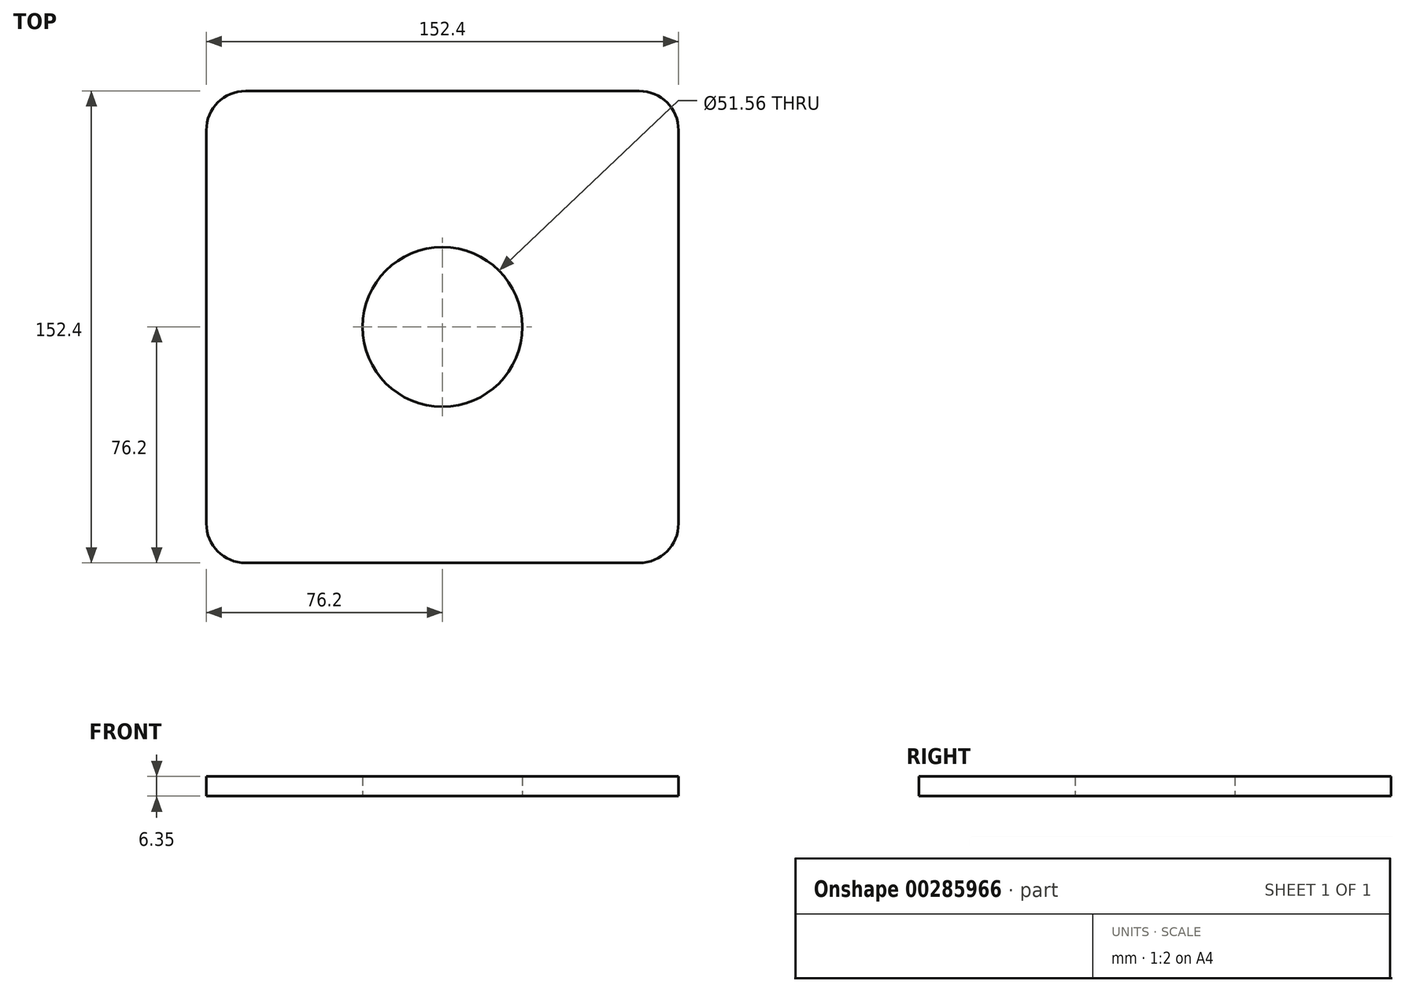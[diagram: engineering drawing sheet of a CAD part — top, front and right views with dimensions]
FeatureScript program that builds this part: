
annotation { "Feature Type Name" : "Feature", "Feature Type Description" : "" }
export const myFeature = defineFeature(function(context is Context, id is Id, definition is map)
    precondition{}
    {
        {
            var Q0;
            Q0=qCreatedBy(makeId("Top.planeOp"),FACE);
            var sketch = newSketch(context, id + "F0", { "sketchPlane" : qUnion([Q0])});
            skLineSegment(sketch, "E0.bottom", {"start": v(12.7, 0) * mm, "end": v(139.7, 0) * mm});
            skLineSegment(sketch, "E0.top", {"start": v(12.7, -152.4) * mm, "end": v(139.7, -152.4) * mm});
            skLineSegment(sketch, "E0.left", {"start": v(0, -12.7) * mm, "end": v(0, -139.7) * mm});
            skLineSegment(sketch, "E0.right", {"start": v(152.4, -12.7) * mm, "end": v(152.4, -139.7) * mm});
            skPoint(sketch, "E1.visualSharp", {"position": v(0, 0) * mm});
            skArc(sketch, "E1.filletArc", {"start": v(12.7, 0) * mm, "mid": v(3.72, -3.72) * mm, "end": v(0, -12.7) * mm});
            skPoint(sketch, "E2.visualSharp", {"position": v(152.4, 0) * mm});
            skArc(sketch, "E2.filletArc", {"start": v(152.4, -12.7) * mm, "mid": v(148.68, -3.72) * mm, "end": v(139.7, 0) * mm});
            skPoint(sketch, "E3.visualSharp", {"position": v(152.4, -152.4) * mm});
            skArc(sketch, "E3.filletArc", {"start": v(139.7, -152.4) * mm, "mid": v(148.68, -148.68) * mm, "end": v(152.4, -139.7) * mm});
            skPoint(sketch, "E4.visualSharp", {"position": v(0, -152.4) * mm});
            skArc(sketch, "E4.filletArc", {"start": v(0, -139.7) * mm, "mid": v(3.72, -148.68) * mm, "end": v(12.7, -152.4) * mm});
            skLineSegment(sketch, "E5", {"start": v(76.2, 0) * mm, "end": v(76.2, -152.4) * mm});
            skCircle(sketch, "E6", {"center": v(76.2, -76.2) * mm, "radius": 25.78 * mm});
            skSolve(sketch);
        }
        {
            var Q0;
            Q0 = qSketchRegion(id + "F0", true);
            extrude(context, id + "F1", {"entities" : qUnion([Q0]), "depth" : 6.35 * mm});
        }
    });
